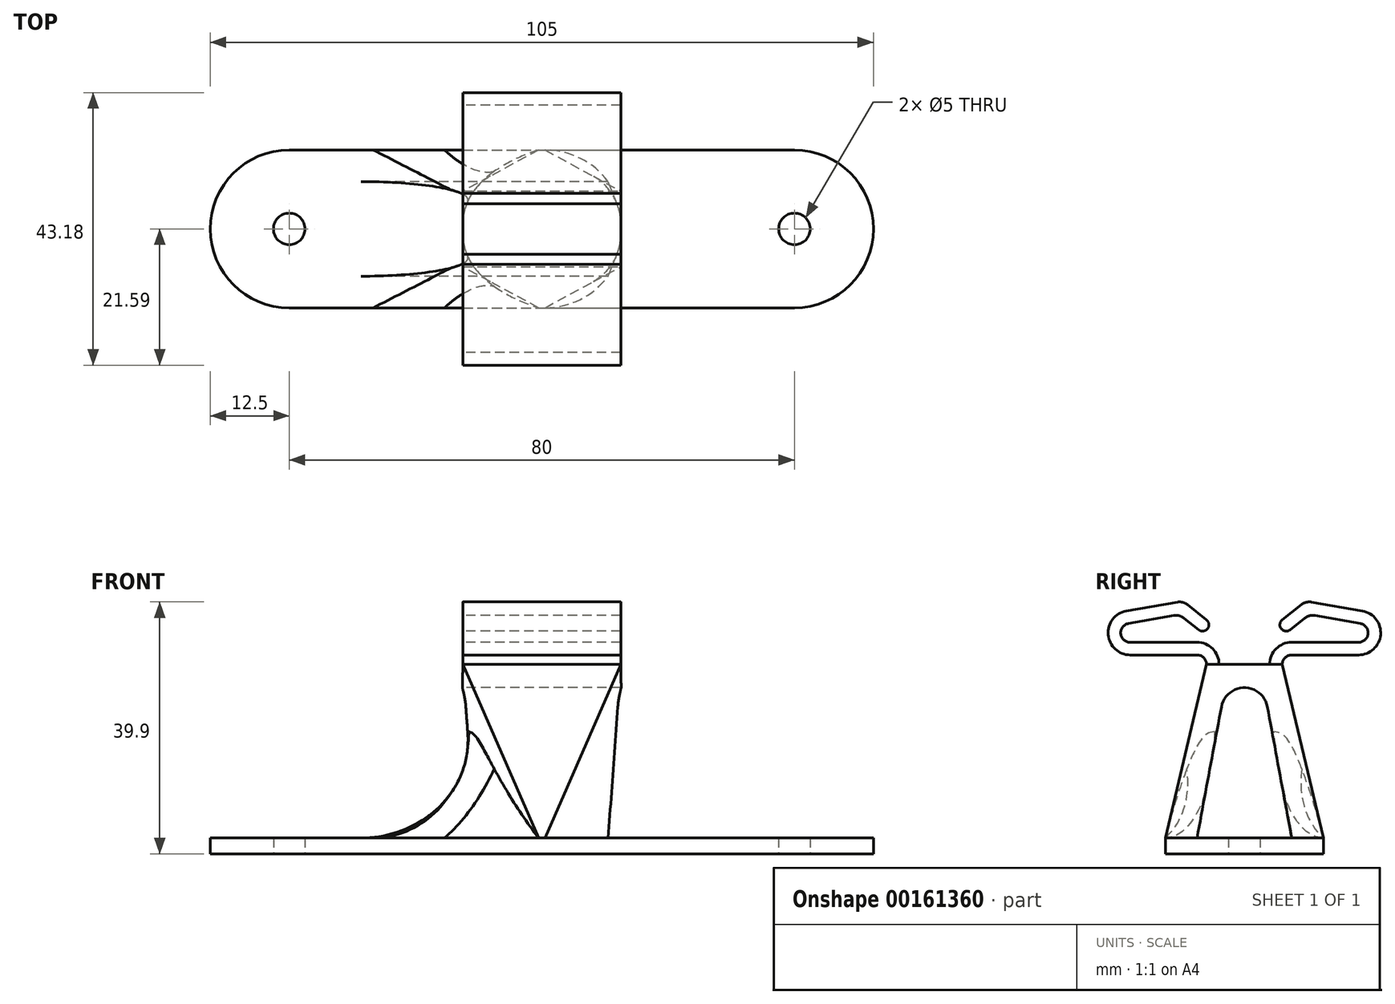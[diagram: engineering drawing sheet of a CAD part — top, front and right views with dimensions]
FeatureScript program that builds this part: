
annotation { "Feature Type Name" : "Feature", "Feature Type Description" : "" }
export const myFeature = defineFeature(function(context is Context, id is Id, definition is map)
    precondition{}
    {
        {
            var Q0;
            Q0=qCreatedBy(makeId("Top.planeOp"),FACE);
            var sketch = newSketch(context, id + "F0", { "sketchPlane" : qUnion([Q0])});
            skLineSegment(sketch, "E0", {"start": v(0, 0) * mm, "end": v(80, 0) * mm, "construction": true});
            skCircle(sketch, "E1", {"center": v(0, 0) * mm, "radius": 2.5 * mm});
            skCircle(sketch, "E2", {"center": v(80, 0) * mm, "radius": 2.5 * mm});
            skArc(sketch, "E3", {"start": v(0, 12.5) * mm, "mid": v(-12.5, 0) * mm, "end": v(0, -12.5) * mm});
            skArc(sketch, "E4", {"start": v(80, -12.5) * mm, "mid": v(92.5, 0) * mm, "end": v(80, 12.5) * mm});
            skLineSegment(sketch, "E5.bottom", {"start": v(0, 12.5) * mm, "end": v(80, 12.5) * mm});
            skLineSegment(sketch, "E5.top", {"start": v(0, -12.5) * mm, "end": v(80, -12.5) * mm});
            skCircle(sketch, "E6", {"center": v(40, 0) * mm, "radius": 12.5 * mm});
            skSolve(sketch);
        }
        {
            var Q0;
            Q0=makeQuery(id+"F0.imprint","IMPRINT",FACE,{"disambiguationData":[TD([[makeQuery(id+"F0.imprint","IMPRINT",EDGE,{"derivedFrom":sQuery(id+"F0.wireOp",EDGE,"E1")}),-1.0]])]});
            var Q1;
            Q1=makeQuery(id+"F0.imprint","IMPRINT",FACE,{"disambiguationData":[TD([[makeQuery(id+"F0.imprint","IMPRINT",EDGE,{"derivedFrom":sQuery(id+"F0.wireOp",EDGE,"E2")}),-1.0]])]});
            var Q2;
            {var subQ0=sQuery(id+"F0.wireOp",EDGE,"E6");var subQ1=makeQuery(id+"F0.imprint","INTERSECT",VERTEX,{"derivedFrom":[sQuery(id+"F0.wireOp",EDGE,"E5.bottom"),subQ0]});Q2=makeQuery(id+"F0.imprint","IMPRINT",FACE,{"disambiguationData":[TD([[makeQuery(id+"F0.imprint","IMPRINT",EDGE,{"disambiguationData":[TD([[subQ1,-1.0]])],"derivedFrom":subQ0}),1.0]])]});}
            extrude(context, id + "F1", {"entities" : qUnion([Q0, Q1, Q2]), "depth" : 2.5 * mm});
        }
        {
            var Q0;
            Q0=qCreatedBy(makeId("Top.planeOp"),FACE);
            cPlane(context, id + "F2", {"entities" : qUnion([Q0]), "cplaneType" : CPlaneType.OFFSET, "offset" : 30 * mm, "width" : 150 * mm, "height" : 150 * mm});
        }
        {
            var Q0;
            Q0=qCreatedBy(id+"F2.planeOp",FACE);
            var sketch = newSketch(context, id + "F3", { "sketchPlane" : qUnion([Q0])});
            skLineSegment(sketch, "E7.bottom", {"start": v(27.5, 6) * mm, "end": v(52.5, 6) * mm});
            skLineSegment(sketch, "E7.top", {"start": v(27.5, -6) * mm, "end": v(52.5, -6) * mm});
            skLineSegment(sketch, "E7.left", {"start": v(27.5, 6) * mm, "end": v(27.5, -6) * mm});
            skLineSegment(sketch, "E7.right", {"start": v(52.5, 6) * mm, "end": v(52.5, -6) * mm});
            skPoint(sketch, "E8", {"position": v(52.5, 0) * mm});
            skSolve(sketch);
        }
        {
            var Q0;
            Q0=sQuery(id+"F0.wireOp",VERTEX,"E6.center");
            var Q1;
            Q1=qCreatedBy(makeId("Right.planeOp"),FACE);
            cPlane(context, id + "F4", {"entities" : qUnion([Q0, Q1]), "cplaneType" : CPlaneType.PLANE_POINT, "offset" : 25 * mm, "width" : 150 * mm, "height" : 150 * mm});
        }
        {
            var Q0;
            Q0=makeQuery(id+"F1.opExtrude","CAP_FACE",FACE,{"disambiguationData":[OSD([sQuery(id+"F0.wireOp",EDGE,"E1"),sQuery(id+"F0.wireOp",EDGE,"E2"),sQuery(id+"F0.wireOp",EDGE,"E3"),sQuery(id+"F0.wireOp",EDGE,"E4"),sQuery(id+"F0.wireOp",EDGE,"E5.bottom"),sQuery(id+"F0.wireOp",EDGE,"E5.top")])],"isStart":false});
            var sketch = newSketch(context, id + "F5", { "sketchPlane" : qUnion([Q0])});
            skLineSegment(sketch, "E9", {"start": v(40, 12.5) * mm, "end": v(40, -12.5) * mm, "construction": true});
            skLineSegment(sketch, "E10.bottom", {"start": v(39.5, 12.5) * mm, "end": v(40.5, 12.5) * mm});
            skLineSegment(sketch, "E10.top", {"start": v(39.5, -12.5) * mm, "end": v(40.5, -12.5) * mm});
            skLineSegment(sketch, "E10.left", {"start": v(39.5, 12.5) * mm, "end": v(39.5, -12.5) * mm, "construction": true});
            skLineSegment(sketch, "E10.right", {"start": v(40.5, 12.5) * mm, "end": v(40.5, -12.5) * mm, "construction": true});
            skArc(sketch, "E11", {"start": v(40.5, 12.5) * mm, "mid": v(53, 0) * mm, "end": v(40.5, -12.5) * mm});
            skArc(sketch, "E12", {"start": v(39.5, 12.5) * mm, "mid": v(27, 0) * mm, "end": v(39.5, -12.5) * mm});
            skSolve(sketch);
        }
        {
            var Q1;
            Q1=makeQuery(id+"F5.imprint","IMPRINT",FACE,{"disambiguationData":[TD([[makeQuery(id+"F5.imprint","IMPRINT",EDGE,{"derivedFrom":sQuery(id+"F5.wireOp",EDGE,"E10.bottom")}),-1.0]])]});
            var Q2;
            Q2=makeQuery(id+"F3.imprint","IMPRINT",FACE,{"disambiguationData":[TD([[makeQuery(id+"F3.imprint","IMPRINT",EDGE,{"derivedFrom":sQuery(id+"F3.wireOp",EDGE,"E7.bottom")}),-1.0]])]});
            loft(context, id + "F6", {"operationType" : NewBodyOperationType.ADD, "sheetProfilesArray" : [{ "sheetProfileEntities" : qUnion([Q1]) }, { "sheetProfileEntities" : qUnion([Q2]) }]});
        }
        {
            var Q0;
            Q0=makeQuery(id+"F6.opLoft","MID_CAP_EDGE",EDGE,{"disambiguationData":[OSD([sQuery(id+"F0.wireOp",EDGE,"E5.bottom"),sQuery(id+"F0.wireOp",EDGE,"E5.top"),sQuery(id+"F5.wireOp",EDGE,"E10.bottom"),sQuery(id+"F5.wireOp",EDGE,"E10.top"),sQuery(id+"F5.wireOp",EDGE,"E11")])],"capPos":0.0});
            var Q1;
            Q1=makeQuery(id+"F6.opLoft","MID_CAP_EDGE",EDGE,{"disambiguationData":[OSD([sQuery(id+"F0.wireOp",EDGE,"E5.bottom"),sQuery(id+"F0.wireOp",EDGE,"E5.top"),sQuery(id+"F5.wireOp",EDGE,"E10.bottom"),sQuery(id+"F5.wireOp",EDGE,"E10.top"),sQuery(id+"F5.wireOp",EDGE,"E12")])],"capPos":0.0});
            fillet(context, id + "F7", {"entities" : qUnion([Q0, Q1]), "radius" : 17 * mm, "tangentPropagation" : true, "allowEdgeOverflow" : false});
        }
        {
            var Q0;
            Q0=qCreatedBy(id+"F4.planeOp",FACE);
            var sketch = newSketch(context, id + "F8", { "sketchPlane" : qUnion([Q0])});
            skArc(sketch, "E13", {"start": v(18.09, 33.5) * mm, "mid": v(19.58, 34.87) * mm, "end": v(18.35, 36.48) * mm});
            skLineSegment(sketch, "E14", {"start": v(18.35, 36.48) * mm, "end": v(10.27, 37.9) * mm});
            skLineSegment(sketch, "E15", {"start": v(9.73, 40.03) * mm, "end": v(18.7, 38.45) * mm});
            skArc(sketch, "E16", {"start": v(18.7, 38.45) * mm, "mid": v(21.57, 34.7) * mm, "end": v(18.09, 31.5) * mm});
            skPoint(sketch, "E17.start.orphan", {"position": v(0, 41) * mm});
            skPoint(sketch, "E18.end.orphan", {"position": v(0, 39) * mm});
            skLineSegment(sketch, "E19", {"start": v(18.09, 33.5) * mm, "end": v(7.5, 33.5) * mm});
            skLineSegment(sketch, "E20", {"start": v(18.09, 31.5) * mm, "end": v(7.5, 31.5) * mm});
            skArc(sketch, "E21", {"start": v(7.5, 31.5) * mm, "mid": v(6.44, 31.06) * mm, "end": v(6, 30) * mm});
            skArc(sketch, "E22", {"start": v(7.5, 33.5) * mm, "mid": v(5.03, 32.47) * mm, "end": v(4, 30) * mm});
            skLineSegment(sketch, "E23", {"start": v(4, 30) * mm, "end": v(6, 30) * mm});
            skLineSegment(sketch, "E24", {"start": v(0, 42.07) * mm, "end": v(0, 50.34) * mm, "construction": true});
            skLineSegment(sketch, "E25", {"start": v(0, 0) * mm, "end": v(0, 41.7) * mm, "construction": true});
            skLineSegment(sketch, "E26", {"start": v(0, 41.7) * mm, "end": v(27.22, 41.7) * mm, "construction": true});
            skLineSegment(sketch, "E27.MirrorCS", {"start": v(-4, 30) * mm, "end": v(-6, 30) * mm});
            skLineSegment(sketch, "E28.MirrorCS", {"start": v(-18.09, 31.5) * mm, "end": v(-7.5, 31.5) * mm});
            skArc(sketch, "E29.MirrorCS", {"start": v(-7.5, 31.5) * mm, "mid": v(-6.44, 31.06) * mm, "end": v(-6, 30) * mm});
            skLineSegment(sketch, "E30.MirrorCS", {"start": v(-18.35, 36.48) * mm, "end": v(-10.27, 37.9) * mm});
            skLineSegment(sketch, "E31.MirrorCS", {"start": v(0, 41.7) * mm, "end": v(-27.22, 41.7) * mm, "construction": true});
            skArc(sketch, "E32.MirrorCS", {"start": v(-18.09, 33.5) * mm, "mid": v(-19.58, 34.87) * mm, "end": v(-18.35, 36.48) * mm});
            skArc(sketch, "E33.MirrorCS", {"start": v(-18.7, 38.45) * mm, "mid": v(-21.57, 34.7) * mm, "end": v(-18.09, 31.5) * mm});
            skLineSegment(sketch, "E34.MirrorCS", {"start": v(-18.09, 33.5) * mm, "end": v(-7.5, 33.5) * mm});
            skArc(sketch, "E35.MirrorCS", {"start": v(-7.5, 33.5) * mm, "mid": v(-5.03, 32.47) * mm, "end": v(-4, 30) * mm});
            skLineSegment(sketch, "E36.MirrorCS", {"start": v(-9.73, 40.03) * mm, "end": v(-18.7, 38.45) * mm});
            skLineSegment(sketch, "E37", {"start": v(-9.73, 40.03) * mm, "end": v(-6, 37.05) * mm});
            skLineSegment(sketch, "E38", {"start": v(-6, 37.05) * mm, "end": v(-7.24, 35.48) * mm, "construction": true});
            skLineSegment(sketch, "E39", {"start": v(-7.24, 35.48) * mm, "end": v(-10.27, 37.9) * mm});
            skPoint(sketch, "E40.orphan", {"position": v(-8.5, 40.24) * mm});
            skPoint(sketch, "E41.orphan", {"position": v(-8.5, 38.21) * mm});
            skArc(sketch, "E42", {"start": v(-7.24, 35.48) * mm, "mid": v(-5.83, 35.64) * mm, "end": v(-6, 37.05) * mm});
            skLineSegment(sketch, "E43.MirrorCS", {"start": v(7.24, 35.48) * mm, "end": v(10.27, 37.9) * mm});
            skArc(sketch, "E44.MirrorCS", {"start": v(7.24, 35.48) * mm, "mid": v(5.83, 35.64) * mm, "end": v(6, 37.05) * mm});
            skLineSegment(sketch, "E45.MirrorCS", {"start": v(9.73, 40.03) * mm, "end": v(6, 37.05) * mm});
            skPoint(sketch, "E46.orphan", {"position": v(8.5, 40.24) * mm});
            skPoint(sketch, "E47.start.orphan", {"position": v(8.5, 38.21) * mm});
            skSolve(sketch);
        }
        {
            var Q0;
            Q0 = qSketchRegion(id + "F8", true);
            extrude(context, id + "F9", {"entities" : qUnion([Q0]), "operationType" : NewBodyOperationType.ADD, "endBound" : BoundingType.SYMMETRIC, "depth" : 25 * mm});
        }
        {
            var Q0;
            Q0=qCreatedBy(makeId("Right.planeOp"),FACE);
            var sketch = newSketch(context, id + "F10", { "sketchPlane" : qUnion([Q0])});
            skLineSegment(sketch, "E48", {"start": v(0, 30.08) * mm, "end": v(0, 0) * mm, "construction": true});
            skLineSegment(sketch, "E49", {"start": v(-7.5, 2.5) * mm, "end": v(7.5, 2.5) * mm});
            skLineSegment(sketch, "E50", {"start": v(7.5, 2.5) * mm, "end": v(3.63, 23.3) * mm});
            skLineSegment(sketch, "E51", {"start": v(-3.63, 23.3) * mm, "end": v(-7.5, 2.5) * mm});
            skPoint(sketch, "E52", {"position": v(0, 22.63) * mm});
            skPoint(sketch, "E53", {"position": v(0, 2.5) * mm});
            skArc(sketch, "E54", {"start": v(-3.63, 23.3) * mm, "mid": v(0, 26.32) * mm, "end": v(3.63, 23.3) * mm});
            skSolve(sketch);
        }
        {
            var Q0;
            Q0=makeQuery(id+"F10.imprint","IMPRINT",FACE,{"disambiguationData":[TD([[makeQuery(id+"F10.imprint","IMPRINT",EDGE,{"derivedFrom":sQuery(id+"F10.wireOp",EDGE,"E49")}),1.0]])]});
            extrude(context, id + "F11", {"entities" : qUnion([Q0]), "operationType" : NewBodyOperationType.REMOVE, "endBound" : BoundingType.THROUGH_ALL, "depth" : 25 * mm});
        }
        {
            var Q0;
            Q0=makeQuery(id+"F9.opExtrude","SWEPT_EDGE",EDGE,{"disambiguationData":[OSD([sQuery(id+"F8.wireOp",EDGE,"E36.MirrorCS"),sQuery(id+"F8.wireOp",EDGE,"E37")])]});
            var Q1;
            Q1=makeQuery(id+"F9.opExtrude","SWEPT_EDGE",EDGE,{"disambiguationData":[OSD([sQuery(id+"F8.wireOp",EDGE,"E30.MirrorCS"),sQuery(id+"F8.wireOp",EDGE,"E39")])]});
            var Q2;
            Q2=makeQuery(id+"F9.opExtrude","SWEPT_EDGE",EDGE,{"disambiguationData":[OSD([sQuery(id+"F8.wireOp",EDGE,"E14"),sQuery(id+"F8.wireOp",EDGE,"E43.MirrorCS")])]});
            var Q3;
            Q3=makeQuery(id+"F9.opExtrude","SWEPT_EDGE",EDGE,{"disambiguationData":[OSD([sQuery(id+"F8.wireOp",EDGE,"E15"),sQuery(id+"F8.wireOp",EDGE,"E45.MirrorCS")])]});
            fillet(context, id + "F12", {"entities" : qUnion([Q0, Q1, Q2, Q3]), "radius" : 2 * mm, "tangentPropagation" : true, "allowEdgeOverflow" : false});
        }
    });
